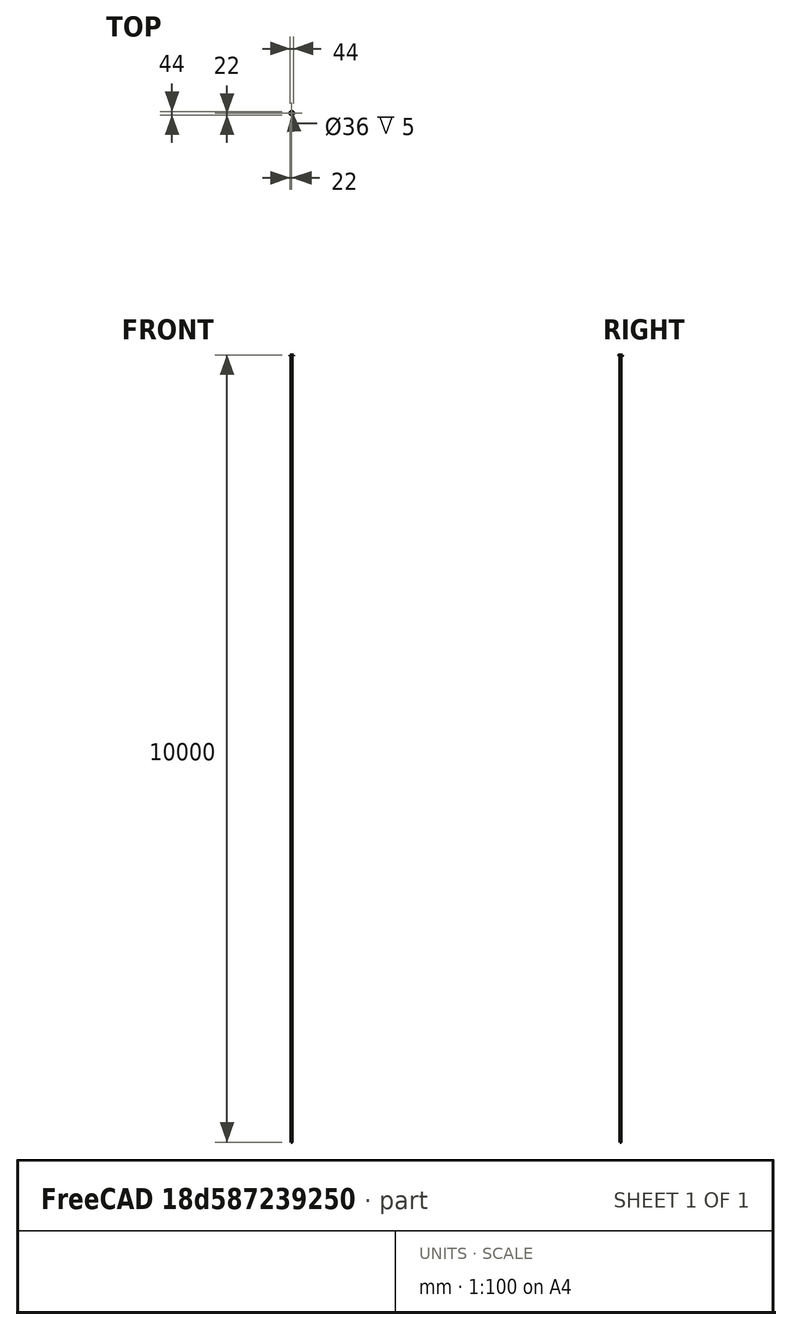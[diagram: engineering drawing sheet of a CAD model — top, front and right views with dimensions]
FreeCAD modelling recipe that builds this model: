
FCSTD DOCUMENT  (FreeCAD 0.16R)
Label: broachpullerbush
License: All rights reserved
LicenseURL: http://en.wikipedia.org/wiki/All_rights_reserved
objects: Sketcher::SketchObject×5, PartDesign::Pocket×3, PartDesign::Pad×2, Mesh::Feature×1
note: 15 computed .brp shape members not serialized (recipe doc carries the construction recipe); baked Part::Feature solids carry a one-line shape summary decoded from their .brp

FEATURE [Sketcher::SketchObject] Sketch
  sketch-geometry (1):
    g0: Circle CenterX=0 CenterY=0 CenterZ=0 NormalX=0 NormalY=0 NormalZ=1 Radius=22
  constraints (2):
    c: Coincident(g0,g-1)
    c: Radius(g0) = 22
FEATURE [PartDesign::Pad] Pad
  Length = 14
  Length2 = 100
  Sketch = -> Sketch
  Type = 0
FEATURE [Sketcher::SketchObject] Sketch001
  Placement = pos=(0,0,14) rot=(0,0,1;0rad)
  Support = -> Pad [Face3]
  sketch-geometry (1):
    g0: Circle CenterX=0 CenterY=0 CenterZ=0 NormalX=0 NormalY=0 NormalZ=1 Radius=18
  constraints (2):
    c: Coincident(g0,g-1)
    c: Radius(g0) = 18
FEATURE [PartDesign::Pocket] Pocket
  Length = 5
  Sketch = -> Sketch001
  Type = 0
FEATURE [Sketcher::SketchObject] Sketch002
  Placement = pos=(0,0,9) rot=(0,0,1;0rad)
  Support = -> Pocket [Face5]
  sketch-geometry (1):
    g0: Circle CenterX=0 CenterY=0 CenterZ=0 NormalX=0 NormalY=0 NormalZ=1 Radius=12.6
  constraints (2):
    c: Coincident(g0,g-1)
    c: Radius(g0) = 12.6
FEATURE [PartDesign::Pad] Pad001
  Length = 5
  Length2 = 100
  Sketch = -> Sketch002
  Type = 0
FEATURE [Sketcher::SketchObject] Sketch003
  Placement = pos=(0,0,14) rot=(0,0,1;0rad)
  Support = -> Pad001 [Face7]
  sketch-geometry (1):
    g0: Circle CenterX=0 CenterY=0 CenterZ=0 NormalX=0 NormalY=0 NormalZ=1 Radius=6.45
  constraints (2):
    c: Coincident(g0,g-1)
    c: Radius(g0) = 6.45
FEATURE [PartDesign::Pocket] Pocket001
  Length = 5
  Sketch = -> Sketch003
  Type = 1
FEATURE [Sketcher::SketchObject] Sketch004
  Placement = pos=(0,0,0) rot=(1,0,0;3.14159rad)
  Support = -> Pocket001 [Face2]
  sketch-geometry (1):
    g0: Circle CenterX=0 CenterY=0 CenterZ=0 NormalX=0 NormalY=0 NormalZ=1 Radius=16.2
  constraints (2):
    c: Radius(g0) = 16.2
    c: Coincident(g0,g-1)
FEATURE [PartDesign::Pocket] Pocket002
  Length = 8
  Sketch = -> Sketch004
  Type = 0
FEATURE [Mesh::Feature] Mesh  label="Pocket002 (Meshed)"
